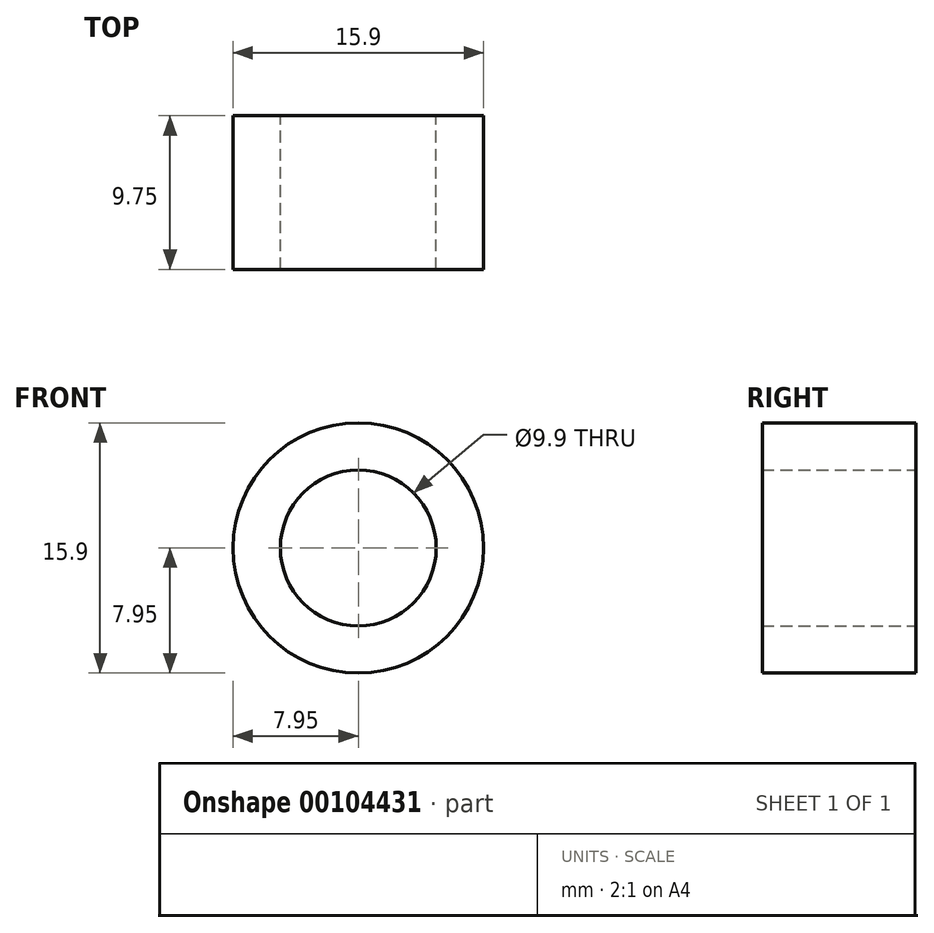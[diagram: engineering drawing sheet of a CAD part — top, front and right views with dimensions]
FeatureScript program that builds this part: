
annotation { "Feature Type Name" : "Feature", "Feature Type Description" : "" }
export const myFeature = defineFeature(function(context is Context, id is Id, definition is map)
    precondition{}
    {
        {
            var Q0;
            Q0=qCreatedBy(makeId("Front.planeOp"),FACE);
            var sketch = newSketch(context, id + "F0", { "sketchPlane" : qUnion([Q0])});
            skCircle(sketch, "E0", {"center": v(0, 0) * mm, "radius": 7.95 * mm});
            skCircle(sketch, "E1", {"center": v(0, 0) * mm, "radius": 4.95 * mm});
            skSolve(sketch);
        }
        {
            var Q0;
            Q0=makeQuery(id+"F0.imprint","IMPRINT",FACE,{"disambiguationData":[TD([[makeQuery(id+"F0.imprint","IMPRINT",EDGE,{"derivedFrom":sQuery(id+"F0.wireOp",EDGE,"E0")}),1.0]])]});
            extrude(context, id + "F1", {"entities" : qUnion([Q0]), "depth" : 9.75 * mm});
        }
    });
